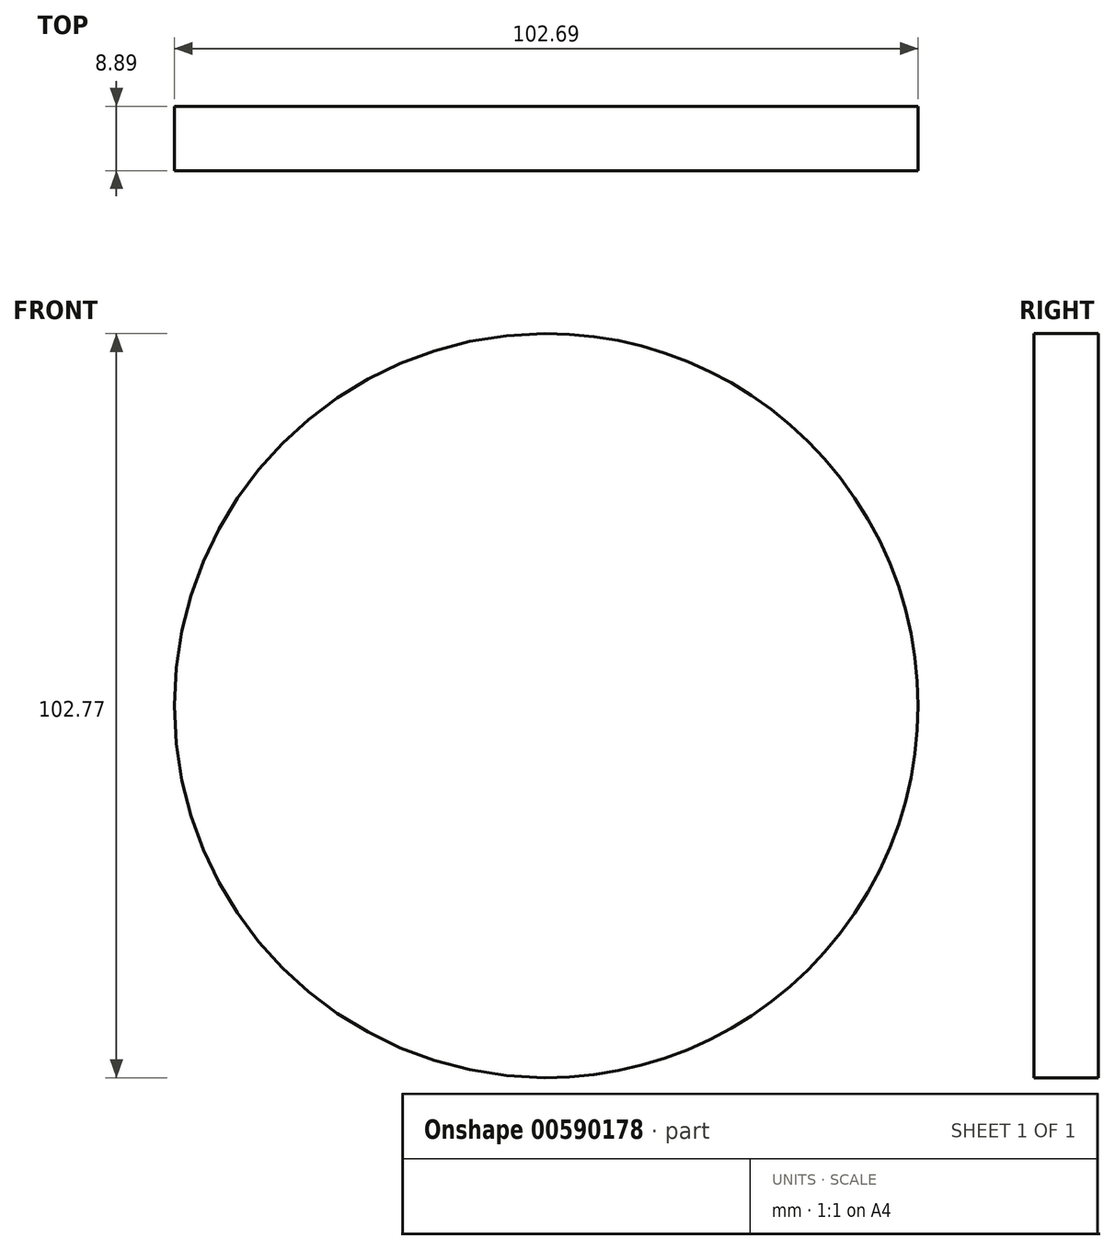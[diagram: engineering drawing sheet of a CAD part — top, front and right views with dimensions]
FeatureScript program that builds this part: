
annotation { "Feature Type Name" : "Feature", "Feature Type Description" : "" }
export const myFeature = defineFeature(function(context is Context, id is Id, definition is map)
    precondition{}
    {
        {
            var Q0;
            Q0=qCreatedBy(makeId("Front.planeOp"),FACE);
            var sketch = newSketch(context, id + "F0", { "sketchPlane" : qUnion([Q0])});
            skArc(sketch, "E0", {"start": v(6.6, -58.28) * mm, "mid": v(58.2, -6.9) * mm, "end": v(6.6, 44.5) * mm});
            skArc(sketch, "E1", {"start": v(6.6, 44.5) * mm, "mid": v(-44.49, -6.9) * mm, "end": v(6.6, -58.28) * mm});
            skSolve(sketch);
        }
        {
            var Q0;
            Q0=qSketchRegion(id+"F0",true);
            extrude(context, id + "F1", {"entities" : qUnion([Q0]), "depth" : 8.9 * mm, "offsetDistance" : 25.4 * mm});
        }
    });
